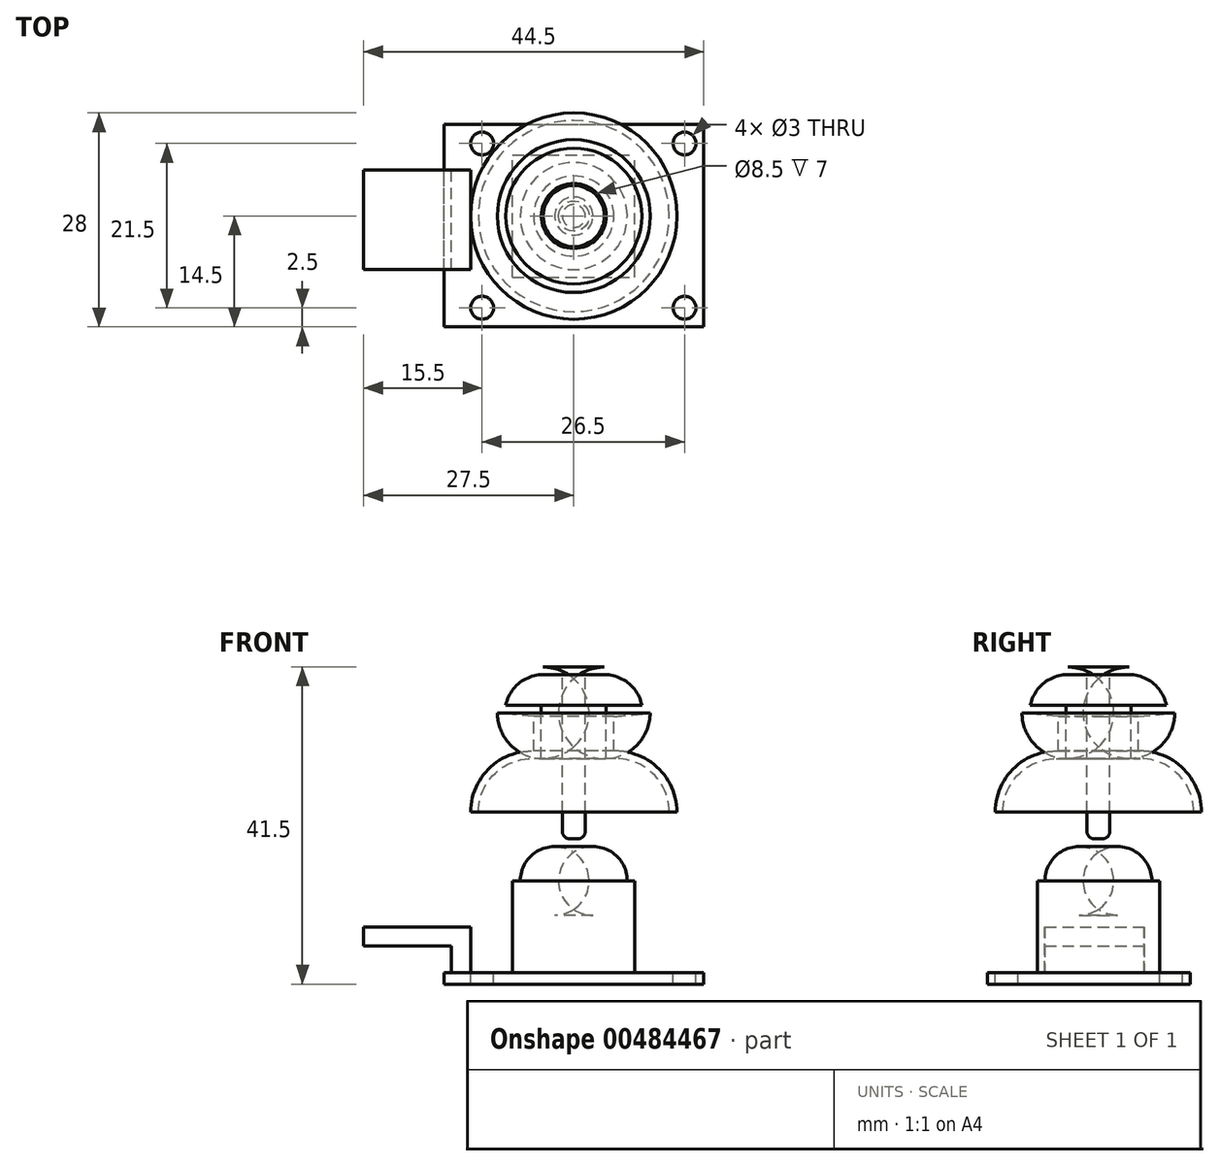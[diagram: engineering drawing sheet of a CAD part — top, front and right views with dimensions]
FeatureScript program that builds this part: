
annotation { "Feature Type Name" : "Feature", "Feature Type Description" : "" }
export const myFeature = defineFeature(function(context is Context, id is Id, definition is map)
    precondition{}
    {
        {
            var Q0;
            Q0=qCreatedBy(makeId("Front.planeOp"),FACE);
            var sketch = newSketch(context, id + "F0", { "sketchPlane" : qUnion([Q0])});
            skLineSegment(sketch, "E0", {"start": v(0, -19) * mm, "end": v(13.5, -19) * mm});
            skLineSegment(sketch, "E1", {"start": v(13.5, -19) * mm, "end": v(13.5, -19) * mm});
            skLineSegment(sketch, "E2", {"start": v(5.5, -11) * mm, "end": v(5.25, -11) * mm});
            skLineSegment(sketch, "E3", {"start": v(5.25, -11) * mm, "end": v(5.25, -6) * mm});
            skLineSegment(sketch, "E4", {"start": v(5.25, -6) * mm, "end": v(10, -6) * mm});
            skLineSegment(sketch, "E5", {"start": v(10, -6) * mm, "end": v(10, -6) * mm});
            skLineSegment(sketch, "E6", {"start": v(4, 0) * mm, "end": v(0, 0) * mm});
            skPoint(sketch, "E7.visualSharp", {"position": v(13.5, -11) * mm});
            skArc(sketch, "E7.filletArc", {"start": v(13.5, -19) * mm, "mid": v(11.16, -13.34) * mm, "end": v(5.5, -11) * mm});
            skPoint(sketch, "E8.visualSharp", {"position": v(10, 0) * mm});
            skArc(sketch, "E8.filletArc", {"start": v(10, -6) * mm, "mid": v(8.24, -1.76) * mm, "end": v(4, 0) * mm});
            skLineSegment(sketch, "E9", {"start": v(0, 0) * mm, "end": v(0, -19) * mm});
            skSolve(sketch);
        }
        {
            var Q0;
            Q0=makeQuery(id+"F0.imprint","IMPRINT",FACE,{"disambiguationData":[TD([[makeQuery(id+"F0.imprint","IMPRINT",EDGE,{"derivedFrom":sQuery(id+"F0.wireOp",EDGE,"E0")}),1.0]])]});
            var Q1;
            Q1=sQuery(id+"F0.wireOp",EDGE,"E9");
            revolve(context, id + "F1", {"entities" : qUnion([Q0]), "axis" : qUnion([Q1]), "revolveType" : RevolveType.FULL});
        }
        {
            var Q0;
            Q0=makeQuery(id+"F1.opRevolve","SWEPT_FACE",FACE,{"disambiguationData":[OSD([sQuery(id+"F0.wireOp",EDGE,"E0")])]});
            shell(context, id + "F2", {"entities" : qUnion([Q0]), "thickness" : 1 * mm});
        }
        {
            var Q0;
            Q0=makeQuery(id+"F2.opShell","OFFSET_FACE",FACE,{"disambiguationData":[OSD([sQuery(id+"F0.wireOp",EDGE,"E6")])]});
            var sketch = newSketch(context, id + "F3", { "sketchPlane" : qUnion([Q0])});
            skCircle(sketch, "E10", {"center": v(0, 0) * mm, "radius": 1.5 * mm});
            skSolve(sketch);
        }
        {
            var Q0;
            Q0=makeQuery(id+"F3.imprint","IMPRINT",FACE,{"disambiguationData":[TD([[makeQuery(id+"F3.imprint","IMPRINT",EDGE,{"derivedFrom":sQuery(id+"F3.wireOp",EDGE,"E10")}),1.0]])]});
            extrude(context, id + "F4", {"entities" : qUnion([Q0]), "operationType" : NewBodyOperationType.ADD, "depth" : 21.5 * mm});
        }
        {
            var Q0;
            Q0=makeQuery(id+"F1.opRevolve","SWEPT_EDGE",EDGE,{"disambiguationData":[OSD([sQuery(id+"F0.wireOp",EDGE,"E3"),sQuery(id+"F0.wireOp",EDGE,"E4")])]});
            chamfer(context, id + "F5", {"entities" : qUnion([Q0]), "chamferType" : ChamferType.TWO_OFFSETS, "width1" : 5 * mm, "oppositeDirection" : false, "width2" : 0.5 * mm, "tangentPropagation" : true});
        }
        {
            var Q0;
            Q0=qCreatedBy(makeId("Front.planeOp"),FACE);
            var sketch = newSketch(context, id + "F6", { "sketchPlane" : qUnion([Q0])});
            skLineSegment(sketch, "E11.bottom", {"start": v(-8, -28) * mm, "end": v(8, -28) * mm});
            skLineSegment(sketch, "E11.top", {"start": v(-8, -40) * mm, "end": v(8, -40) * mm});
            skLineSegment(sketch, "E11.left", {"start": v(-8, -28) * mm, "end": v(-8, -40) * mm});
            skLineSegment(sketch, "E11.right", {"start": v(8, -28) * mm, "end": v(8, -40) * mm});
            skSolve(sketch);
        }
        {
            var Q0;
            Q0=makeQuery(id+"F6.imprint","IMPRINT",FACE,{"disambiguationData":[TD([[makeQuery(id+"F6.imprint","IMPRINT",EDGE,{"derivedFrom":sQuery(id+"F6.wireOp",EDGE,"E11.bottom")}),-1.0]])]});
            extrude(context, id + "F7", {"entities" : qUnion([Q0]), "operationType" : NewBodyOperationType.ADD, "endBound" : BoundingType.SYMMETRIC, "depth" : 16 * mm});
        }
        {
            var Q0;
            Q0=makeQuery(id+"F4.opExtrude","CAP_EDGE",EDGE,{"disambiguationData":[OSD([sQuery(id+"F3.wireOp",EDGE,"E10")])],"isStart":false});
            fillet(context, id + "F8", {"entities" : qUnion([Q0]), "radius" : 1 * mm, "tangentPropagation" : true, "allowEdgeOverflow" : false});
        }
        {
            var Q0;
            Q0=makeQuery(id+"F7.opExtrude","SWEPT_FACE",FACE,{"disambiguationData":[OSD([sQuery(id+"F6.wireOp",EDGE,"E11.top")])]});
            var sketch = newSketch(context, id + "F9", { "sketchPlane" : qUnion([Q0])});
            skLineSegment(sketch, "E12.bottom", {"start": v(-17, 14.5) * mm, "end": v(17, 14.5) * mm});
            skLineSegment(sketch, "E12.top", {"start": v(-17, -12) * mm, "end": v(17, -12) * mm});
            skLineSegment(sketch, "E12.left", {"start": v(-17, 14.5) * mm, "end": v(-17, -12) * mm});
            skLineSegment(sketch, "E12.right", {"start": v(17, 14.5) * mm, "end": v(17, -12) * mm});
            skCircle(sketch, "E13", {"center": v(14.5, 12) * mm, "radius": 1.5 * mm});
            skCircle(sketch, "E14", {"center": v(14.5, -9.5) * mm, "radius": 1.5 * mm});
            skCircle(sketch, "E15", {"center": v(-12, -9.5) * mm, "radius": 1.5 * mm});
            skCircle(sketch, "E16", {"center": v(-12, 12) * mm, "radius": 1.5 * mm});
            skSolve(sketch);
        }
        {
            var Q0;
            Q0=makeQuery(id+"F9.imprint","IMPRINT",FACE,{"disambiguationData":[TD([[makeQuery(id+"F9.imprint","IMPRINT",EDGE,{"derivedFrom":sQuery(id+"F9.wireOp",EDGE,"E12.bottom")}),-1.0]])]});
            var Q1;
            {var subQ0=sQuery(id+"F6.wireOp",EDGE,"E11.top");Q1=makeQuery(id+"F9.imprint","IMPRINT",FACE,{"disambiguationData":[TD([[makeQuery(id+"F9.imprint","IMPRINT",EDGE,{"derivedFrom":makeQuery(id+"F7.opExtrude","CAP_EDGE",EDGE,{"disambiguationData":[OSD([subQ0])],"isStart":true})}),1.0]])]});}
            extrude(context, id + "F10", {"entities" : qUnion([Q0, Q1]), "depth" : 1.5 * mm});
        }
        {
            var Q0;
            Q0=qCreatedBy(makeId("Front.planeOp"),FACE);
            var sketch = newSketch(context, id + "F11", { "sketchPlane" : qUnion([Q0])});
            skLineSegment(sketch, "E17", {"start": v(-13.5, -40) * mm, "end": v(-13.5, -34) * mm});
            skLineSegment(sketch, "E18", {"start": v(-13.5, -34) * mm, "end": v(-27.5, -34) * mm});
            skLineSegment(sketch, "E19", {"start": v(-27.5, -34) * mm, "end": v(-27.5, -36.5) * mm});
            skLineSegment(sketch, "E20", {"start": v(-27.5, -36.5) * mm, "end": v(-16, -36.5) * mm});
            skLineSegment(sketch, "E21", {"start": v(-16, -36.5) * mm, "end": v(-16, -40) * mm});
            skLineSegment(sketch, "E22", {"start": v(-16, -40) * mm, "end": v(-13.5, -40) * mm});
            skSolve(sketch);
        }
        {
            var Q0;
            Q0=makeQuery(id+"F11.imprint","IMPRINT",FACE,{"disambiguationData":[TD([[makeQuery(id+"F11.imprint","IMPRINT",EDGE,{"derivedFrom":sQuery(id+"F11.wireOp",EDGE,"E17")}),1.0]])]});
            extrude(context, id + "F12", {"entities" : qUnion([Q0]), "operationType" : NewBodyOperationType.ADD, "depth" : 7 * mm, "hasSecondDirection" : true, "secondDirectionOppositeDirection" : true, "secondDirectionDepth" : 6 * mm});
        }
        {
            var Q0;
            Q0=makeQuery(id+"F7.opExtrude","SWEPT_FACE",FACE,{"disambiguationData":[OSD([sQuery(id+"F6.wireOp",EDGE,"E11.bottom")])]});
            var sketch = newSketch(context, id + "F13", { "sketchPlane" : qUnion([Q0])});
            skCircle(sketch, "E23", {"center": v(0, 0) * mm, "radius": 7 * mm});
            skSolve(sketch);
        }
        {
            var Q0;
            Q0=makeQuery(id+"F13.imprint","IMPRINT",FACE,{"disambiguationData":[TD([[makeQuery(id+"F13.imprint","IMPRINT",EDGE,{"derivedFrom":sQuery(id+"F13.wireOp",EDGE,"E23")}),1.0]])]});
            extrude(context, id + "F14", {"entities" : qUnion([Q0]), "operationType" : NewBodyOperationType.REMOVE, "oppositeDirection" : true, "depth" : 4.5 * mm});
        }
        {
            var Q0;
            Q0=makeQuery(id+"F14.boolean.opBoolean","COPY",EDGE,{"derivedFrom":makeQuery(id+"F14.opExtrude","CAP_EDGE",EDGE,{"disambiguationData":[OSD([sQuery(id+"F13.wireOp",EDGE,"E23")])],"isStart":false})});
            fillet(context, id + "F15", {"entities" : qUnion([Q0]), "radius" : 4.5 * mm, "tangentPropagation" : true, "allowEdgeOverflow" : false});
        }
    });
